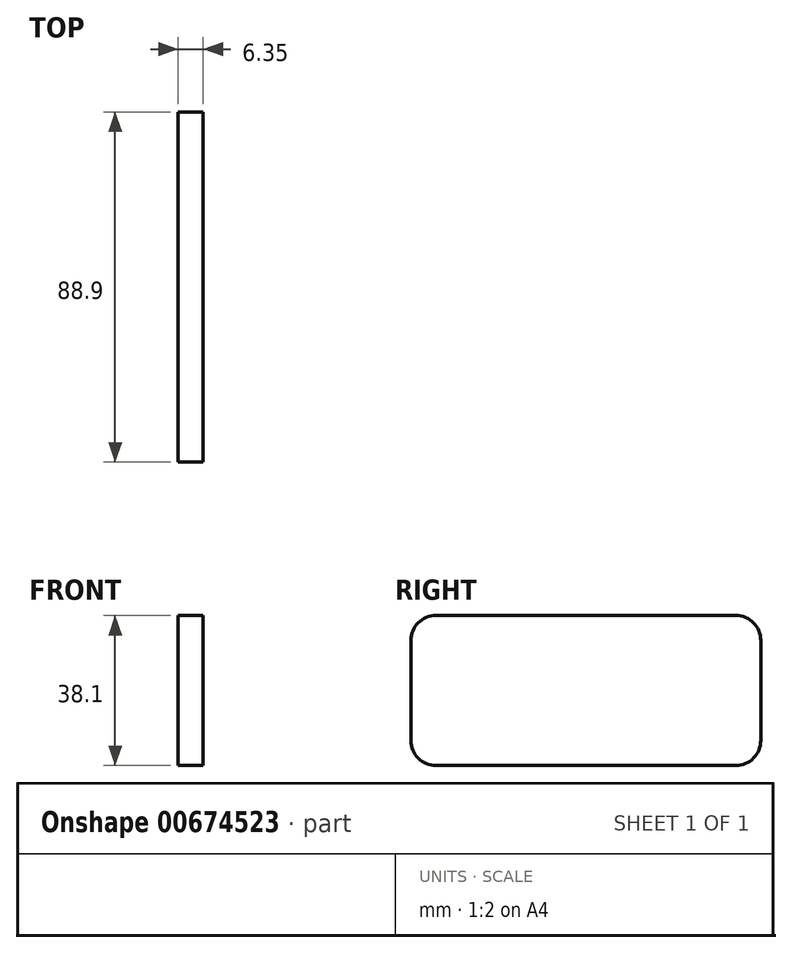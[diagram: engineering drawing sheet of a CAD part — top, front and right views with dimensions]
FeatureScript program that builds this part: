
annotation { "Feature Type Name" : "Feature", "Feature Type Description" : "" }
export const myFeature = defineFeature(function(context is Context, id is Id, definition is map)
    precondition{}
    {
        {
            var Q0;
            Q0=qCreatedBy(makeId("Right.planeOp"),FACE);
            var sketch = newSketch(context, id + "F0", { "sketchPlane" : qUnion([Q0])});
            skLineSegment(sketch, "E0.bottom", {"start": v(38.1, 19.05) * mm, "end": v(-38.1, 19.05) * mm});
            skLineSegment(sketch, "E0.top", {"start": v(38.1, -19.05) * mm, "end": v(-38.1, -19.05) * mm});
            skLineSegment(sketch, "E0.left", {"start": v(44.45, 12.7) * mm, "end": v(44.45, -12.7) * mm});
            skLineSegment(sketch, "E0.right", {"start": v(-44.45, 12.7) * mm, "end": v(-44.45, -12.7) * mm});
            skPoint(sketch, "E0.middle", {"position": v(0, 0) * mm});
            skPoint(sketch, "E1.visualSharp", {"position": v(44.45, 19.05) * mm});
            skArc(sketch, "E1.filletArc", {"start": v(44.45, 12.7) * mm, "mid": v(42.6, 17.2) * mm, "end": v(38.1, 19.05) * mm});
            skPoint(sketch, "E2.visualSharp", {"position": v(44.45, -19.05) * mm});
            skArc(sketch, "E2.filletArc", {"start": v(38.1, -19.05) * mm, "mid": v(42.6, -17.2) * mm, "end": v(44.45, -12.7) * mm});
            skPoint(sketch, "E3.visualSharp", {"position": v(-44.45, -19.05) * mm});
            skArc(sketch, "E3.filletArc", {"start": v(-44.45, -12.7) * mm, "mid": v(-42.6, -17.2) * mm, "end": v(-38.1, -19.05) * mm});
            skPoint(sketch, "E4.visualSharp", {"position": v(-44.45, 19.05) * mm});
            skArc(sketch, "E4.filletArc", {"start": v(-38.1, 19.05) * mm, "mid": v(-42.6, 17.2) * mm, "end": v(-44.45, 12.7) * mm});
            skSolve(sketch);
        }
        {
            var Q0;
            Q0 = qSketchRegion(id + "F0", true);
            extrude(context, id + "F1", {"entities" : qUnion([Q0]), "depth" : 6.35 * mm, "offsetDistance" : 25.4 * mm});
        }
    });
